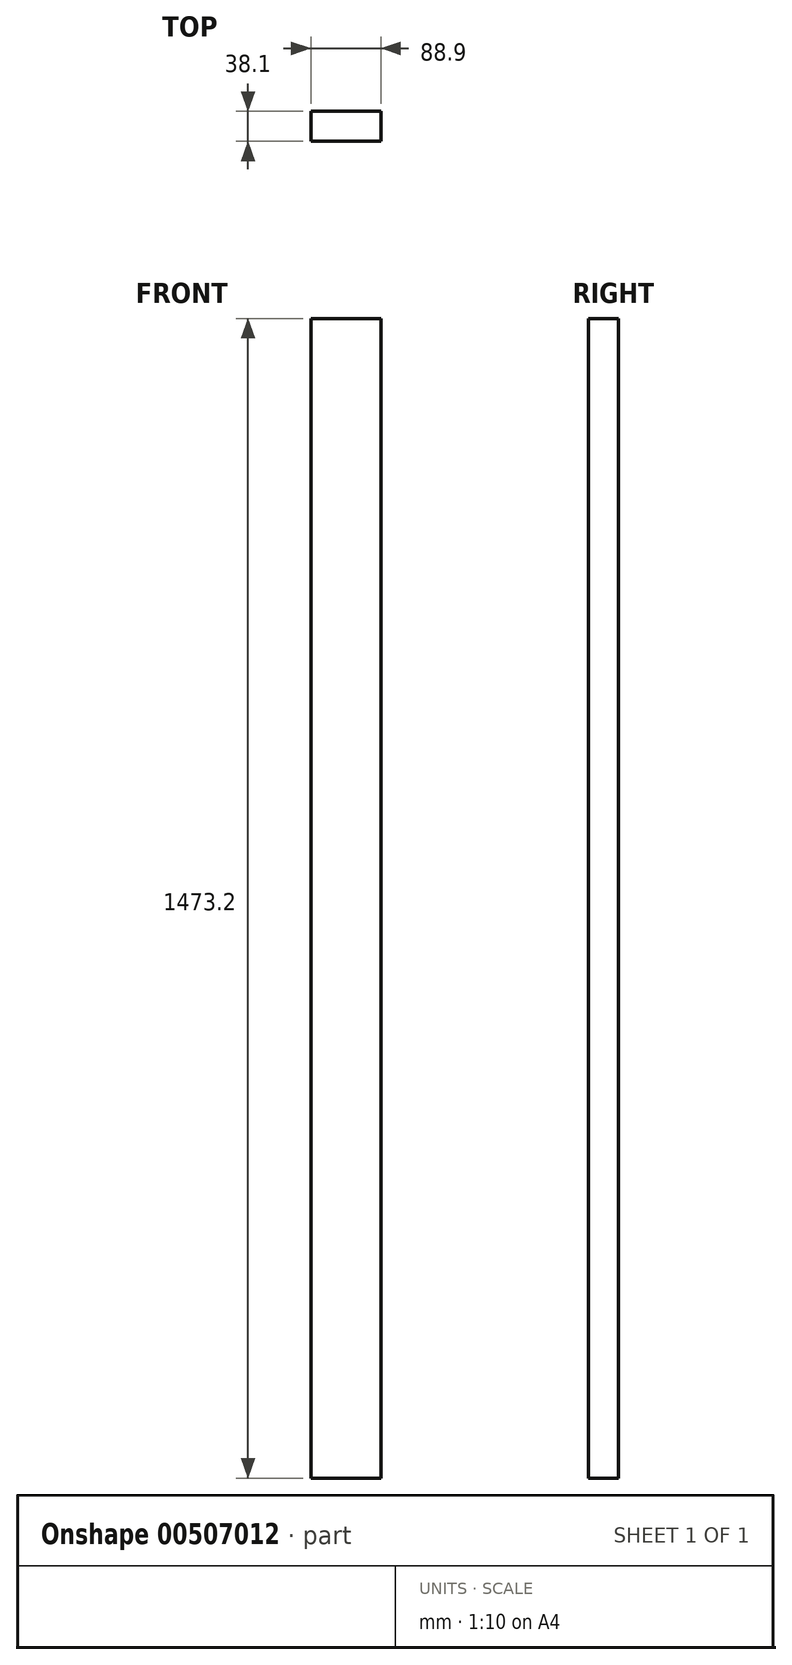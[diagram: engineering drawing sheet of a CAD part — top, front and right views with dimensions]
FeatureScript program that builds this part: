
annotation { "Feature Type Name" : "Feature", "Feature Type Description" : "" }
export const myFeature = defineFeature(function(context is Context, id is Id, definition is map)
    precondition{}
    {
        {
            var Q0;
            Q0=qCreatedBy(makeId("Top.planeOp"),FACE);
            var sketch = newSketch(context, id + "F0", { "sketchPlane" : qUnion([Q0])});
            skLineSegment(sketch, "E0", {"start": v(0, 0) * mm, "end": v(0, 38.1) * mm});
            skLineSegment(sketch, "E1", {"start": v(0, 38.1) * mm, "end": v(88.9, 38.1) * mm});
            skLineSegment(sketch, "E2", {"start": v(88.9, 38.1) * mm, "end": v(88.9, 0) * mm});
            skLineSegment(sketch, "E3", {"start": v(88.9, 0) * mm, "end": v(0, 0) * mm});
            skSolve(sketch);
        }
        {
            var Q0;
            Q0 = qSketchRegion(id + "F0", true);
            extrude(context, id + "F1", {"entities" : qUnion([Q0]), "depth" : 1473.2 * mm});
        }
    });
